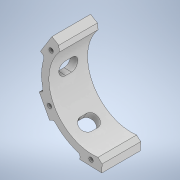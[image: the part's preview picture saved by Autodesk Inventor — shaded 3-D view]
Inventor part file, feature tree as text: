
AUTODESK INVENTOR PART (.ipt)
format: ipt  version: 2020 (Build 240168000, 168)  size: 248,832 bytes
history: native  units: mm
features: plane x4, other x3, sketch x2, extrude x2, chamfer x1, mirror x1, reference x1, projected_geometry x1
ambient origin geometry x8: Origin, YZ Plane, XZ Plane, XY Plane, X Axis, Y Axis, Z Axis, Center Point
bodies: Solid1 (feature_tree)
feature tree (15):
  plane  "Work Plane1"
  sketch  "Sketch1"  dims[d0=60.0mm d1=10.0mm d2=0.0mm d3=3.0mm d4=2.0mm d5=45.0deg]
  plane  "Work Plane2"
  extrude  "Extrusion1"  Depth=10.0mm TaperAngle=0.0deg
  chamfer  "Chamfer1"  Distance=3.0mm Angle=45.0deg
  plane  "Work Plane3"
  extrude  "Extrusion2"  Depth=9.0mm
  plane  "Work Plane4"
  mirror  "Mirror1"
  reference  "Reference1"
  sketch  "Sketch2"  dims[d6=2.0mm d7=9.0mm d8=10.0mm d9=0.0mm]
  projected_geometry  "Projected Loop1"
  parser-record x1  (decoder bookkeeping rows leaked as tree rows — omitted from the tree; the rows remain in map.json)
  other  "reducer_leg.iam"
  other  "motor_h_4:1"
note: 1 file-system path scrubbed to <path> (originals preserved in map.json)
